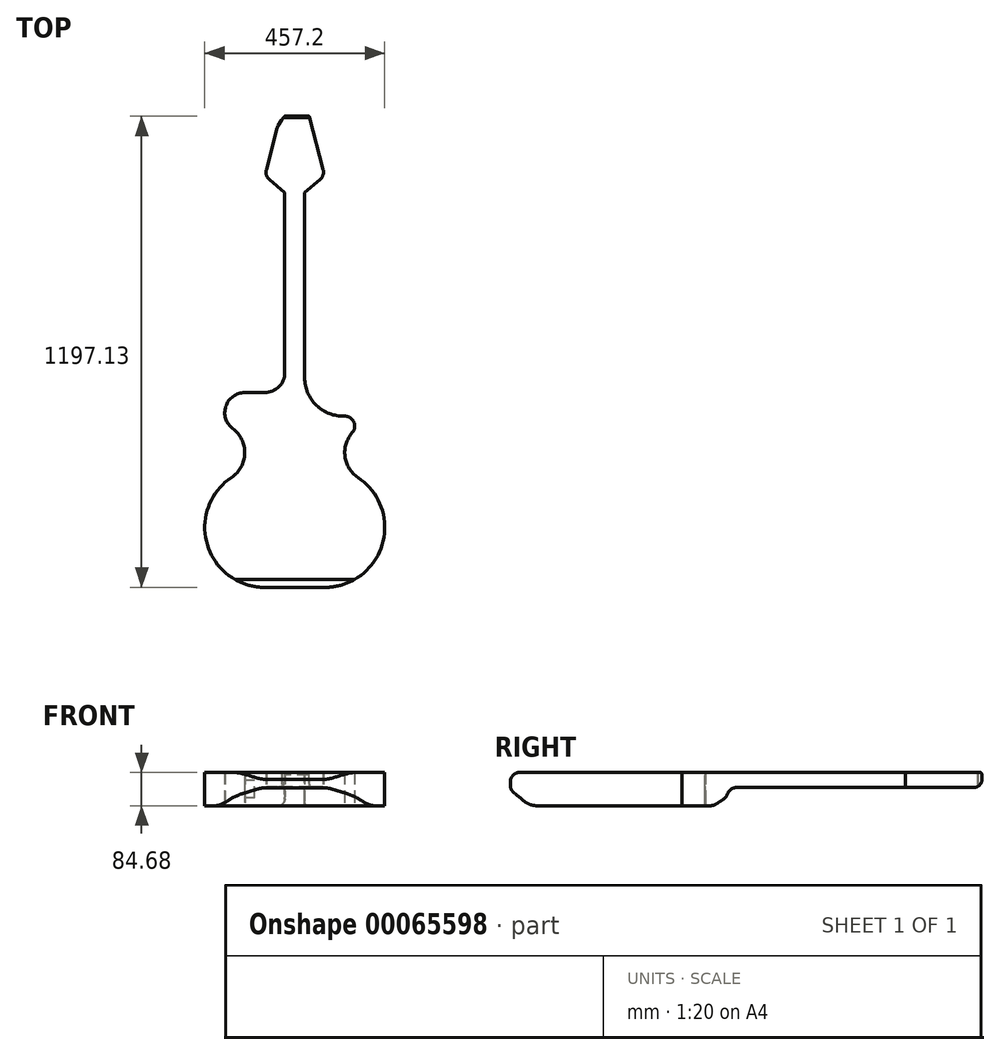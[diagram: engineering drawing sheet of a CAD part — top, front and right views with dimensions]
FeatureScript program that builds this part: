
annotation { "Feature Type Name" : "Feature", "Feature Type Description" : "" }
export const myFeature = defineFeature(function(context is Context, id is Id, definition is map)
    precondition{}
    {
        {
            var Q0;
            Q0=qCreatedBy(makeId("Top.planeOp"),FACE);
            var sketch = newSketch(context, id + "F0", { "sketchPlane" : qUnion([Q0])});
            skArc(sketch, "E0", {"start": v(-84.67, 126.72) * mm, "mid": v(-145.84, -44.24) * mm, "end": v(0, -152.4) * mm});
            skLineSegment(sketch, "E1", {"start": v(0, -152.4) * mm, "end": v(152.4, -152.4) * mm});
            skArc(sketch, "E2", {"start": v(152.4, -152.4) * mm, "mid": v(302.6, -25.77) * mm, "end": v(203.2, 143.68) * mm});
            skArc(sketch, "E3", {"start": v(-84.67, 126.72) * mm, "mid": v(-50.83, 188) * mm, "end": v(-81.28, 251.04) * mm});
            skArc(sketch, "E4", {"start": v(222.25, 240.48) * mm, "mid": v(203.84, 180.23) * mm, "end": v(237.07, 126.72) * mm});
            skLineSegment(sketch, "E5", {"start": v(0, -152.4) * mm, "end": v(-50.8, -152.4) * mm, "construction": true});
            skLineSegment(sketch, "E6", {"start": v(-50.8, -152.4) * mm, "end": v(-50.8, 466.41) * mm, "construction": true});
            skLineSegment(sketch, "E7", {"start": v(152.4, -152.4) * mm, "end": v(203.2, -152.4) * mm, "construction": true});
            skLineSegment(sketch, "E8", {"start": v(203.2, -152.4) * mm, "end": v(203.2, 482.12) * mm, "construction": true});
            skArc(sketch, "E9", {"start": v(-50.8, 342.48) * mm, "mid": v(-99, 307.74) * mm, "end": v(-81.28, 251.04) * mm});
            skLineSegment(sketch, "E10", {"start": v(76.2, -152.4) * mm, "end": v(76.2, 1017.86) * mm, "construction": true});
            skLineSegment(sketch, "E11", {"start": v(-50.8, 342.48) * mm, "end": v(0, 342.48) * mm});
            skLineSegment(sketch, "E12", {"start": v(50.8, 393.28) * mm, "end": v(50.8, 850.48) * mm});
            skLineSegment(sketch, "E13", {"start": v(50.8, 850.48) * mm, "end": v(12.1, 883.5) * mm});
            skLineSegment(sketch, "E14", {"start": v(4, 909.2) * mm, "end": v(31.17, 1013.93) * mm});
            skLineSegment(sketch, "E15", {"start": v(34.4, 1021.28) * mm, "end": v(42.78, 1034.33) * mm});
            skPoint(sketch, "E16.visualSharp", {"position": v(0, 893.82) * mm});
            skArc(sketch, "E16.filletArc", {"start": v(4, 909.2) * mm, "mid": v(4.35, 895.2) * mm, "end": v(12.1, 883.5) * mm});
            skPoint(sketch, "E17.visualSharp", {"position": v(32.2, 1017.86) * mm});
            skArc(sketch, "E17.filletArc", {"start": v(34.4, 1021.28) * mm, "mid": v(32.5, 1017.73) * mm, "end": v(31.17, 1013.93) * mm});
            skPoint(sketch, "E18.visualSharp", {"position": v(52.8, 1049.91) * mm});
            skArc(sketch, "E19.MirrorCS", {"start": v(148.4, 909.2) * mm, "mid": v(148.05, 895.2) * mm, "end": v(140.3, 883.5) * mm});
            skLineSegment(sketch, "E20.MirrorCS", {"start": v(148.4, 909.2) * mm, "end": v(121.23, 1013.93) * mm});
            skLineSegment(sketch, "E21.MirrorCS", {"start": v(101.6, 379.97) * mm, "end": v(101.6, 850.48) * mm});
            skLineSegment(sketch, "E22.MirrorCS", {"start": v(101.6, 850.48) * mm, "end": v(140.3, 883.5) * mm});
            skArc(sketch, "E23", {"start": v(222.25, 240.48) * mm, "mid": v(226.17, 268.13) * mm, "end": v(202.32, 282.66) * mm});
            skArc(sketch, "E24", {"start": v(101.6, 379.97) * mm, "mid": v(131.63, 309.64) * mm, "end": v(203.2, 282.7) * mm});
            skPoint(sketch, "E25.orphan", {"position": v(101.6, 342.48) * mm});
            skPoint(sketch, "E26.visualSharp", {"position": v(50.8, 342.48) * mm});
            skArc(sketch, "E26.filletArc", {"start": v(0, 342.48) * mm, "mid": v(35.92, 357.36) * mm, "end": v(50.8, 393.28) * mm});
            skPoint(sketch, "E27.MirrorCS.end.orphan", {"position": v(109.62, 1034.33) * mm});
            skPoint(sketch, "E27.MirrorCS.start.orphan", {"position": v(118, 1021.28) * mm});
            skPoint(sketch, "E28.MirrorCS.end.orphan", {"position": v(76.2, 1017.86) * mm});
            skPoint(sketch, "E28.MirrorCS.start.orphan", {"position": v(88.68, 1034.95) * mm});
            skPoint(sketch, "E18.filletArc.start.orphan", {"position": v(63.72, 1034.95) * mm});
            skLineSegment(sketch, "E29", {"start": v(42.78, 1034.33) * mm, "end": v(64.78, 1064.82) * mm});
            skLineSegment(sketch, "E30", {"start": v(109.95, 1056.37) * mm, "end": v(148.4, 909.2) * mm});
            skPoint(sketch, "E31.visualSharp", {"position": v(96.33, 1108.53) * mm});
            skArc(sketch, "E31.filletArc", {"start": v(109.95, 1056.37) * mm, "mid": v(90.05, 1074.92) * mm, "end": v(64.78, 1064.82) * mm});
            skSolve(sketch);
        }
        {
            var Q0;
            Q0=qSketchRegion(id+"F0",true);
            extrude(context, id + "F1", {"entities" : qUnion([Q0]), "depth" : 101.6 * mm});
        }
        {
            var Q0;
            Q0=qCreatedBy(makeId("Right.planeOp"),FACE);
            var sketch = newSketch(context, id + "F2", { "sketchPlane" : qUnion([Q0])});
            skLineSegment(sketch, "E32.top", {"start": v(1024.73, 63.19) * mm, "end": v(422.02, 63.19) * mm});
            skPoint(sketch, "E33.visualSharp", {"position": v(397.02, 63.19) * mm});
            skArc(sketch, "E33.filletArc", {"start": v(422.02, 63.19) * mm, "mid": v(407.27, 58.47) * mm, "end": v(398, 46.06) * mm});
            skLineSegment(sketch, "E34", {"start": v(387.8, 33.02) * mm, "end": v(369.24, 21) * mm});
            skLineSegment(sketch, "E35", {"start": v(355.43, 16.92) * mm, "end": v(-86.24, 16.92) * mm});
            skLineSegment(sketch, "E36", {"start": v(-118.59, 28.56) * mm, "end": v(-144.25, 49.75) * mm});
            skLineSegment(sketch, "E37", {"start": v(-153.47, 69.34) * mm, "end": v(-153.47, 76.6) * mm});
            skLineSegment(sketch, "E38", {"start": v(-128.07, 102) * mm, "end": v(1038.38, 102) * mm});
            skLineSegment(sketch, "E39", {"start": v(1044.73, 95.65) * mm, "end": v(1044.73, 83.19) * mm});
            skPoint(sketch, "E40.visualSharp", {"position": v(396.64, 38.74) * mm});
            skArc(sketch, "E40.filletArc", {"start": v(387.8, 33.02) * mm, "mid": v(394, 38.69) * mm, "end": v(398, 46.06) * mm});
            skPoint(sketch, "E41.visualSharp", {"position": v(362.94, 16.92) * mm});
            skArc(sketch, "E41.filletArc", {"start": v(355.43, 16.92) * mm, "mid": v(362.63, 17.96) * mm, "end": v(369.24, 21) * mm});
            skPoint(sketch, "E42.visualSharp", {"position": v(-104.5, 16.92) * mm});
            skArc(sketch, "E42.filletArc", {"start": v(-118.59, 28.56) * mm, "mid": v(-103.43, 19.92) * mm, "end": v(-86.24, 16.92) * mm});
            skPoint(sketch, "E43.visualSharp", {"position": v(-153.47, 102) * mm});
            skArc(sketch, "E43.filletArc", {"start": v(-128.07, 102) * mm, "mid": v(-137.36, 100.24) * mm, "end": v(-145.36, 95.2) * mm});
            skPoint(sketch, "E44.visualSharp", {"position": v(-153.47, 76.6) * mm});
            skArc(sketch, "E44.filletArc", {"start": v(-145.36, 95.2) * mm, "mid": v(-151.36, 86.75) * mm, "end": v(-153.47, 76.6) * mm});
            skPoint(sketch, "E45.visualSharp", {"position": v(-153.47, 57.37) * mm});
            skArc(sketch, "E45.filletArc", {"start": v(-153.47, 69.34) * mm, "mid": v(-151.05, 58.51) * mm, "end": v(-144.25, 49.75) * mm});
            skPoint(sketch, "E46.visualSharp", {"position": v(1044.73, 102) * mm});
            skArc(sketch, "E46.filletArc", {"start": v(1044.73, 95.65) * mm, "mid": v(1042.87, 100.14) * mm, "end": v(1038.38, 102) * mm});
            skPoint(sketch, "E47.visualSharp", {"position": v(1044.73, 63.19) * mm});
            skArc(sketch, "E47.filletArc", {"start": v(1024.73, 63.19) * mm, "mid": v(1038.87, 69.05) * mm, "end": v(1044.73, 83.19) * mm});
            skLineSegment(sketch, "E48.bottom", {"start": v(-172.35, -72.65) * mm, "end": v(1084.67, -72.65) * mm});
            skLineSegment(sketch, "E48.top", {"start": v(-172.35, 117.01) * mm, "end": v(1084.67, 117.01) * mm});
            skLineSegment(sketch, "E48.left", {"start": v(-172.35, -72.65) * mm, "end": v(-172.35, 117.01) * mm});
            skLineSegment(sketch, "E48.right", {"start": v(1084.67, -72.65) * mm, "end": v(1084.67, 117.01) * mm});
            skSolve(sketch);
        }
        {
            var Q0;
            Q0=makeQuery(id+"F2.imprint","IMPRINT",FACE,{"disambiguationData":[TD([[makeQuery(id+"F2.imprint","IMPRINT",EDGE,{"derivedFrom":sQuery(id+"F2.wireOp",EDGE,"E32.top")}),1.0]])]});
            extrude(context, id + "F3", {"entities" : qUnion([Q0]), "operationType" : NewBodyOperationType.REMOVE, "endBound" : BoundingType.THROUGH_ALL, "depth" : 25.4 * mm});
        }
        {
            var Q0;
            Q0=qSketchRegion(id+"F2",true);
            extrude(context, id + "F4", {"entities" : qUnion([Q0]), "operationType" : NewBodyOperationType.REMOVE, "endBound" : BoundingType.THROUGH_ALL, "oppositeDirection" : true, "depth" : 25.4 * mm});
        }
        {
            var Q0;
            Q0=makeQuery(id+"F3.boolean.opBoolean","COPY",FACE,{"derivedFrom":makeQuery(id+"F3.opExtrude","SWEPT_FACE",FACE,{"disambiguationData":[OSD([sQuery(id+"F2.wireOp",EDGE,"E39")])]})});
            shell(context, id + "F5", {"entities" : qUnion([Q0]), "thickness" : 1 * mm});
        }
        {
            var Q0;
            Q0=makeQuery(id+"F1.opExtrude","SWEPT_FACE",FACE,{"disambiguationData":[OSD([sQuery(id+"F0.wireOp",EDGE,"E11")])]});
            var sketch = newSketch(context, id + "F6", { "sketchPlane" : qUnion([Q0])});
            skLineSegment(sketch, "E49.bottom", {"start": v(278.49, 31.6) * mm, "end": v(248.86, 31.6) * mm});
            skLineSegment(sketch, "E49.top", {"start": v(278.49, 80.29) * mm, "end": v(248.86, 80.29) * mm});
            skLineSegment(sketch, "E49.left", {"start": v(278.49, 31.6) * mm, "end": v(278.49, 80.29) * mm});
            skLineSegment(sketch, "E49.right", {"start": v(248.86, 31.6) * mm, "end": v(248.86, 80.29) * mm});
            skPoint(sketch, "E50.firstSnap0", {"position": v(25.4, 16.92) * mm});
            skLineSegment(sketch, "E50.bottom", {"start": v(25.4, 36.47) * mm, "end": v(50.8, 36.47) * mm});
            skLineSegment(sketch, "E50.top", {"start": v(25.4, 81.3) * mm, "end": v(50.8, 81.3) * mm});
            skLineSegment(sketch, "E50.left", {"start": v(25.4, 36.47) * mm, "end": v(25.4, 81.3) * mm});
            skLineSegment(sketch, "E50.right", {"start": v(50.8, 36.47) * mm, "end": v(50.8, 81.3) * mm});
            skSolve(sketch);
        }
        {
            var Q0;
            Q0=makeQuery(id+"F6.imprint","IMPRINT",FACE,{"disambiguationData":[TD([[makeQuery(id+"F6.imprint","IMPRINT",EDGE,{"derivedFrom":sQuery(id+"F6.wireOp",EDGE,"E50.bottom")}),1.0]])]});
            extrude(context, id + "F7", {"entities" : qUnion([Q0]), "operationType" : NewBodyOperationType.REMOVE, "oppositeDirection" : true, "depth" : 5 * mm});
        }
    });
